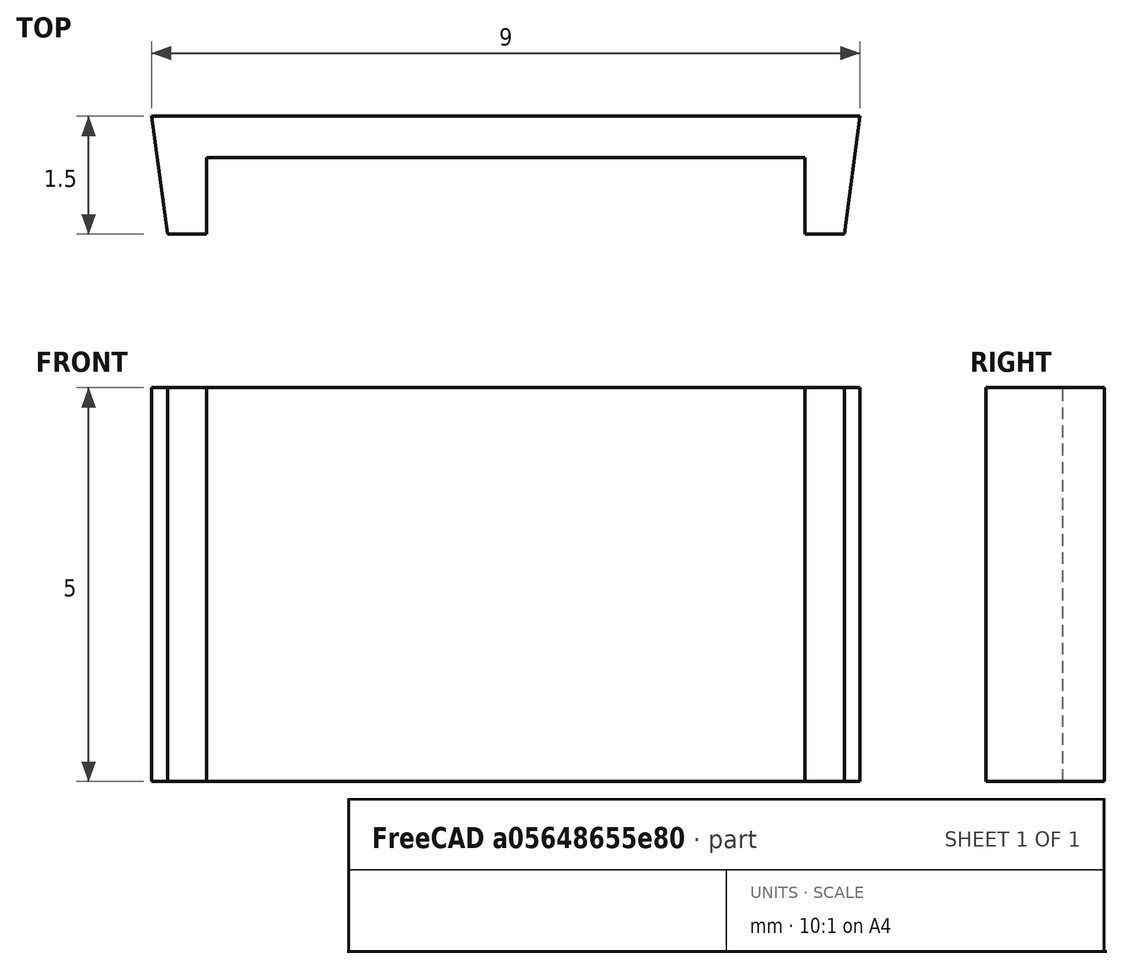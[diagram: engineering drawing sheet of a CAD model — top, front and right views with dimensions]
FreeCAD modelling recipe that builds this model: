
FCSTD DOCUMENT  (FreeCAD 0.19R)
Label: wireCram
License: All rights reserved
LicenseURL: http://en.wikipedia.org/wiki/All_rights_reserved
objects: Sketcher::SketchObject×1, PartDesign::Pad×1, PartDesign::Body×1
note: 4 computed .brp shape members not serialized (recipe doc carries the construction recipe); baked Part::Feature solids carry a one-line shape summary decoded from their .brp

FEATURE [Sketcher::SketchObject] Sketch
  FullyConstrained = false
  MapMode = 5
  Support = -> [XY_Plane]
  sketch-geometry (8):
    g0: LineSegment StartX=0.7 StartY=-1.5 StartZ=0 EndX=0.7 EndY=-0.522979 EndZ=0
    g1: LineSegment StartX=0.7 StartY=-0.522979 StartZ=0 EndX=8.3 EndY=-0.522979 EndZ=0
    g2: LineSegment StartX=8.3 StartY=-0.522979 StartZ=0 EndX=8.3 EndY=-1.5 EndZ=0
    g3: LineSegment StartX=8.3 StartY=-1.5 StartZ=0 EndX=8.8 EndY=-1.5 EndZ=0
    g4: LineSegment StartX=8.8 StartY=-1.5 StartZ=0 EndX=9 EndY=0 EndZ=0
    g5: LineSegment StartX=9 StartY=0 StartZ=0 EndX=0 EndY=0 EndZ=0
    g6: LineSegment StartX=0 StartY=0 StartZ=0 EndX=0.2 EndY=-1.5 EndZ=0
    g7: LineSegment StartX=0.2 StartY=-1.5 StartZ=0 EndX=0.7 EndY=-1.5 EndZ=0
  constraints (22):
    c: Vertical(g0)
    c: Coincident(g0,g1)
    c: Horizontal(g1)
    c: Coincident(g1,g2)
    c: Vertical(g2)
    c: Coincident(g2,g3)
    c: Horizontal(g3)
    c: Coincident(g3,g4)
    c: Coincident(g4,g5)
    c: Horizontal(g5)
    c: Coincident(g5,g6)
    c: Coincident(g6,g7)
    c: Coincident(g7,g0)
    c: Horizontal(g7)
    c: DistanceX(g1,g1) = 7.6
    c: DistanceX(g7,g7) = 0.5
    c: DistanceX(g3,g3) = 0.5
    c: DistanceY(g4,g4) = 1.5
    c: Coincident(g5,g-1)
    c: DistanceX(g5,g5) = 9
    c: DistanceX(g5,g0) = 0.7
    c: DistanceY(g6,g5) = 1.5
FEATURE [PartDesign::Pad] Pad
  Direction = (1,1,1)
  Length = 5
  Length2 = 100
  Profile = -> Sketch
  Type = 0
FEATURE [PartDesign::Body] Body
  Group = -> [Sketch,Pad]
  Origin = -> Origin
  Tip = -> Pad
